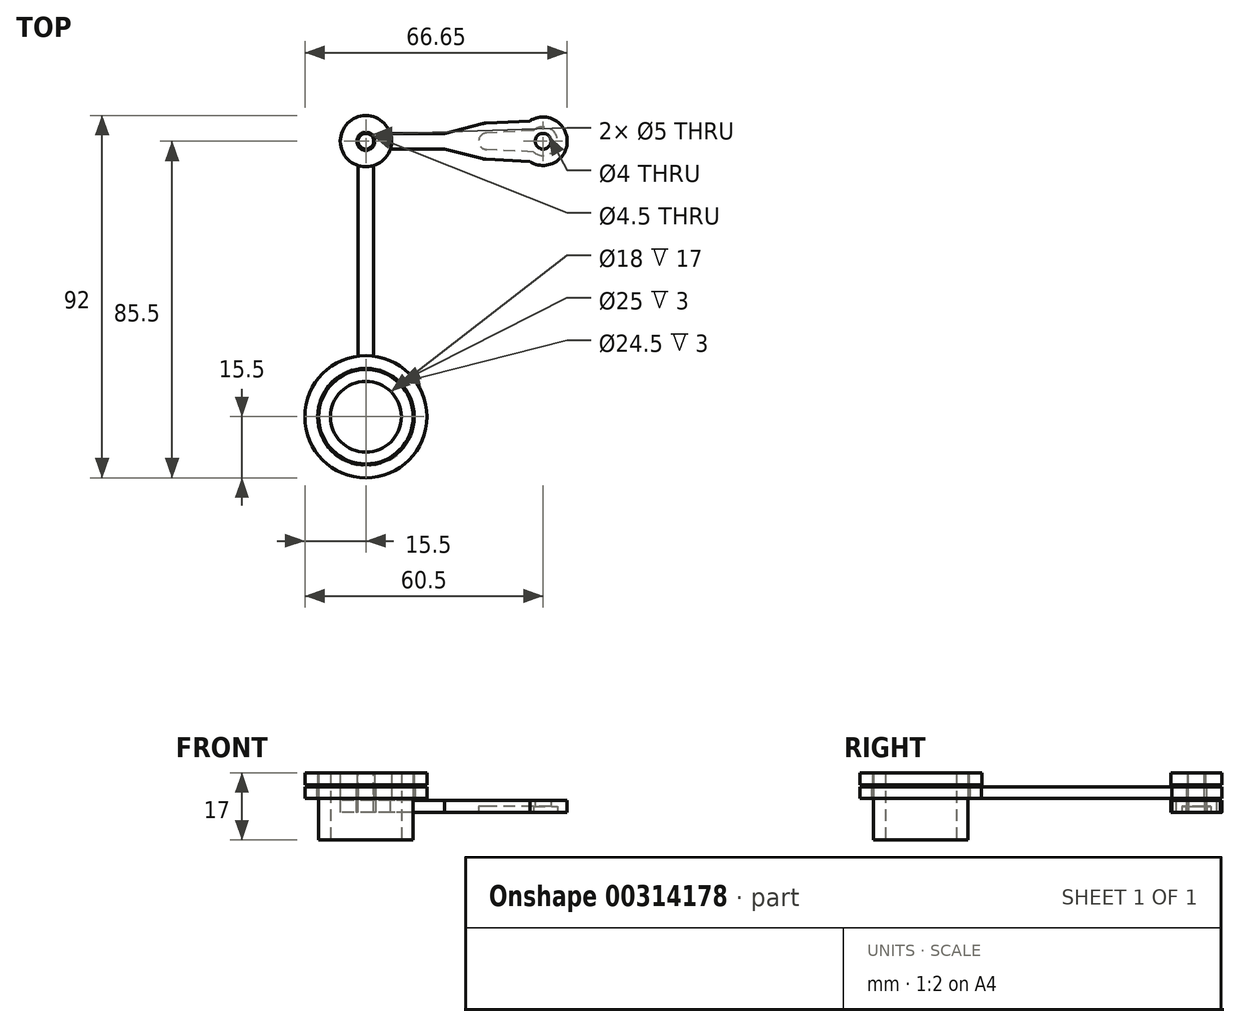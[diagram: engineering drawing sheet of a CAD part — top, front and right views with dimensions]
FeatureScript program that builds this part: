
annotation { "Feature Type Name" : "Feature", "Feature Type Description" : "" }
export const myFeature = defineFeature(function(context is Context, id is Id, definition is map)
    precondition{}
    {
        {
            var Q0;
            Q0=qCreatedBy(makeId("Top.planeOp"),FACE);
            cPlane(context, id + "F0", {"entities" : qUnion([Q0]), "cplaneType" : CPlaneType.OFFSET, "offset" : 3 * mm, "width" : 150 * mm, "height" : 150 * mm});
        }
        {
            var Q0;
            Q0=qCreatedBy(id+"F0.planeOp",FACE);
            cPlane(context, id + "F1", {"entities" : qUnion([Q0]), "cplaneType" : CPlaneType.OFFSET, "offset" : .5 * mm, "width" : 150 * mm, "height" : 150 * mm});
        }
        {
            var Q0;
            Q0=qCreatedBy(id+"F1.planeOp",FACE);
            cPlane(context, id + "F2", {"entities" : qUnion([Q0]), "cplaneType" : CPlaneType.OFFSET, "offset" : 3 * mm, "width" : 150 * mm, "height" : 150 * mm});
        }
        {
            var Q0;
            Q0=qCreatedBy(id+"F2.planeOp",FACE);
            cPlane(context, id + "F3", {"entities" : qUnion([Q0]), "cplaneType" : CPlaneType.OFFSET, "offset" : .5 * mm, "width" : 150 * mm, "height" : 150 * mm});
        }
        {
            var Q0;
            Q0=qCreatedBy(id+"F3.planeOp",FACE);
            cPlane(context, id + "F4", {"entities" : qUnion([Q0]), "cplaneType" : CPlaneType.OFFSET, "offset" : 3 * mm, "width" : 150 * mm, "height" : 150 * mm});
        }
        {
            var Q0;
            Q0=qCreatedBy(makeId("Top.planeOp"),FACE);
            var sketch = newSketch(context, id + "F5", { "sketchPlane" : qUnion([Q0])});
            skArc(sketch, "E0", {"start": v(-2.46, -2.7) * mm, "mid": v(3.65, 0) * mm, "end": v(-2.46, 2.7) * mm});
            skArc(sketch, "E1", {"start": v(-14.36, 2.1) * mm, "mid": v(-16.35, 0) * mm, "end": v(-14.36, -2.1) * mm});
            skPoint(sketch, "E2", {"position": v(-16.35, 0) * mm});
            skPoint(sketch, "E3", {"position": v(3.65, 0) * mm});
            skPoint(sketch, "E4", {"position": v(-2.46, 2.7) * mm});
            skPoint(sketch, "E5.MirrorP", {"position": v(-2.46, -2.7) * mm});
            skLineSegment(sketch, "E6", {"start": v(-2.46, 2.7) * mm, "end": v(-14.36, 2.1) * mm});
            skLineSegment(sketch, "E7", {"start": v(-2.46, -2.7) * mm, "end": v(-14.36, -2.1) * mm});
            skLineSegment(sketch, "E8.0", {"start": v(-3.35, 5.16) * mm, "end": v(-14.48, 4.6) * mm});
            skArc(sketch, "E8.1", {"start": v(-3.35, -5.16) * mm, "mid": v(6.15, 0) * mm, "end": v(-3.35, 5.16) * mm});
            skLineSegment(sketch, "E8.2", {"start": v(-3.35, -5.16) * mm, "end": v(-14.48, -4.6) * mm});
            skArc(sketch, "E8.3", {"start": v(-14.48, 4.6) * mm, "mid": v(-14.94, 4.55) * mm, "end": v(-15.39, 4.46) * mm});
            skLineSegment(sketch, "E9", {"start": v(-25, 0) * mm, "end": v(-25, 2) * mm, "construction": true});
            skLineSegment(sketch, "E10.MirrorCS", {"start": v(-25, 0) * mm, "end": v(-25, -2) * mm, "construction": true});
            skLineSegment(sketch, "E11", {"start": v(-25, 2) * mm, "end": v(-15.39, 4.46) * mm});
            skLineSegment(sketch, "E12", {"start": v(-25, -2) * mm, "end": v(-15.39, -4.46) * mm});
            skCircle(sketch, "E13", {"center": v(-45, 0) * mm, "radius": 2 * mm, "construction": true});
            skLineSegment(sketch, "E14", {"start": v(-25, 2) * mm, "end": v(-38.82, 2) * mm});
            skLineSegment(sketch, "E15.MirrorCS", {"start": v(-25, -2) * mm, "end": v(-38.82, -2) * mm});
            skArc(sketch, "E16.trimOffspring", {"start": v(-15.39, -4.46) * mm, "mid": v(-14.94, -4.55) * mm, "end": v(-14.48, -4.6) * mm});
            skCircle(sketch, "E17", {"center": v(0, 0) * mm, "radius": 2 * mm});
            skCircle(sketch, "E18", {"center": v(-45, 0) * mm, "radius": 2.5 * mm});
            skArc(sketch, "E19", {"start": v(-38.82, 2) * mm, "mid": v(-51.5, 0) * mm, "end": v(-38.82, -2) * mm});
            skArc(sketch, "E20", {"start": v(-38.82, -2) * mm, "mid": v(-38.5, 0) * mm, "end": v(-38.82, 2) * mm, "construction": true});
            skCircle(sketch, "E21", {"center": v(-45, -70) * mm, "radius": 9 * mm});
            skCircle(sketch, "E22", {"center": v(-45, -70) * mm, "radius": 12 * mm});
            skCircle(sketch, "E23", {"center": v(-45, -70) * mm, "radius": 15.5 * mm});
            skLineSegment(sketch, "E24", {"start": v(-45, 0) * mm, "end": v(-45, -70) * mm, "construction": true});
            skLineSegment(sketch, "E25", {"start": v(-47, -6.18) * mm, "end": v(-47, -54.63) * mm, "construction": true});
            skLineSegment(sketch, "E26.MirrorCS", {"start": v(-43, -6.18) * mm, "end": v(-43, -54.63) * mm, "construction": true});
            skCircle(sketch, "E27", {"center": v(-45, -70) * mm, "radius": 12.5 * mm});
            skCircle(sketch, "E28", {"center": v(-45, -70) * mm, "radius": 12.25 * mm, "construction": true});
            skSolve(sketch);
        }
        {
            var Q0;
            Q0=makeQuery(id+"F5.imprint","IMPRINT",FACE,{"disambiguationData":[TD([[makeQuery(id+"F5.imprint","IMPRINT",EDGE,{"derivedFrom":sQuery(id+"F5.wireOp",EDGE,"E0")}),-1.0]])]});
            var Q1;
            Q1=makeQuery(id+"F5.imprint","IMPRINT",FACE,{"disambiguationData":[TD([[makeQuery(id+"F5.imprint","IMPRINT",EDGE,{"derivedFrom":sQuery(id+"F5.wireOp",EDGE,"E0")}),1.0]])]});
            var Q2;
            Q2=qCreatedBy(id+"F0.planeOp",FACE);
            extrude(context, id + "F6", {"entities" : qUnion([Q0, Q1]), "endBound" : BoundingType.UP_TO_SURFACE, "endBoundEntityFace" : qUnion([Q2]), "depth" : 3 * mm});
        }
        {
            var Q0;
            Q0=makeQuery(id+"F5.imprint","IMPRINT",FACE,{"disambiguationData":[TD([[makeQuery(id+"F5.imprint","IMPRINT",EDGE,{"derivedFrom":sQuery(id+"F5.wireOp",EDGE,"E0")}),1.0]])]});
            extrude(context, id + "F7", {"entities" : qUnion([Q0]), "operationType" : NewBodyOperationType.REMOVE, "depth" : 1.5 * mm});
        }
        {
            var Q0;
            Q0=qCreatedBy(id+"F1.planeOp",FACE);
            var sketch = newSketch(context, id + "F8", { "sketchPlane" : qUnion([Q0])});
            skArc(sketch, "E29.0", {"start": v(-38.82, 2) * mm, "mid": v(-49.6, 4.6) * mm, "end": v(-47, -6.18) * mm});
            skArc(sketch, "E29.1", {"start": v(-38.82, -2) * mm, "mid": v(-38.5, 0) * mm, "end": v(-38.82, 2) * mm});
            skLineSegment(sketch, "E29.2", {"start": v(-43, -6.18) * mm, "end": v(-43, -54.63) * mm});
            skLineSegment(sketch, "E29.3", {"start": v(-47, -6.18) * mm, "end": v(-47, -54.63) * mm});
            skArc(sketch, "E29.4", {"start": v(-47, -54.63) * mm, "mid": v(-45, -85.5) * mm, "end": v(-43, -54.63) * mm});
            skArc(sketch, "E30.trimOffspring", {"start": v(-43, -6.18) * mm, "mid": v(-40.4, -4.6) * mm, "end": v(-38.82, -2) * mm});
            skCircle(sketch, "E31.0", {"center": v(-45, 0) * mm, "radius": 2.5 * mm});
            skCircle(sketch, "E32.0", {"center": v(-45, -70) * mm, "radius": 12.5 * mm});
            skSolve(sketch);
        }
        {
            var Q0;
            Q0=makeQuery(id+"F8.imprint","IMPRINT",FACE,{"disambiguationData":[TD([[makeQuery(id+"F8.imprint","IMPRINT",EDGE,{"derivedFrom":sQuery(id+"F8.wireOp",EDGE,"E29.0")}),1.0]])]});
            var Q1;
            Q1=qCreatedBy(id+"F2.planeOp",FACE);
            extrude(context, id + "F9", {"entities" : qUnion([Q0]), "endBound" : BoundingType.UP_TO_SURFACE, "endBoundEntityFace" : qUnion([Q1]), "depth" : 4 * mm});
        }
        {
            var Q0;
            Q0=qCreatedBy(id+"F3.planeOp",FACE);
            var sketch = newSketch(context, id + "F10", { "sketchPlane" : qUnion([Q0])});
            skArc(sketch, "E33.0", {"start": v(-38.82, -2) * mm, "mid": v(-38.5, 0) * mm, "end": v(-38.82, 2) * mm});
            skArc(sketch, "E33.1", {"start": v(-38.82, 2) * mm, "mid": v(-51.5, 0) * mm, "end": v(-38.82, -2) * mm});
            skCircle(sketch, "E33.2", {"center": v(-45, 0) * mm, "radius": 2 * mm});
            skCircle(sketch, "E34", {"center": v(-45, 0) * mm, "radius": 2.25 * mm});
            skSolve(sketch);
        }
        {
            var Q0;
            Q0 = qSketchRegion(id + "F10", true);
            extrude(context, id + "F11", {"entities" : qUnion([Q0]), "depth" : 3 * mm});
        }
        {
            var Q0;
            Q0=makeQuery(id+"F10.imprint","IMPRINT",FACE,{"disambiguationData":[TD([[makeQuery(id+"F10.imprint","IMPRINT",EDGE,{"derivedFrom":sQuery(id+"F10.wireOp",EDGE,"E33.2")}),1.0]])]});
            var Q1;
            Q1=sQuery(id+"F10.wireOp",EDGE,"E33.2");
            var Q2;
            Q2=makeQuery(id+"F6.opExtrude","CAP_FACE",FACE,{"disambiguationData":[OSD([sQuery(id+"F5.wireOp",EDGE,"E8.0"),sQuery(id+"F5.wireOp",EDGE,"E8.1"),sQuery(id+"F5.wireOp",EDGE,"E8.2"),sQuery(id+"F5.wireOp",EDGE,"E8.3"),sQuery(id+"F5.wireOp",EDGE,"E11"),sQuery(id+"F5.wireOp",EDGE,"E12"),sQuery(id+"F5.wireOp",EDGE,"E14"),sQuery(id+"F5.wireOp",EDGE,"E15.MirrorCS"),sQuery(id+"F5.wireOp",EDGE,"E16.trimOffspring"),sQuery(id+"F5.wireOp",EDGE,"E17"),sQuery(id+"F5.wireOp",EDGE,"E18"),sQuery(id+"F5.wireOp",EDGE,"E19")])],"isStart":true});
            extrude(context, id + "F12", {"entities" : qUnion([Q0]), "operationType" : NewBodyOperationType.ADD, "surfaceEntities" : qUnion([Q1]), "endBound" : BoundingType.UP_TO_SURFACE, "oppositeDirection" : true, "endBoundEntityFace" : qUnion([Q2]), "depth" : 25 * mm});
        }
        {
            var Q0;
            Q0=makeQuery(id+"F5.imprint","IMPRINT",FACE,{"disambiguationData":[TD([[makeQuery(id+"F5.imprint","IMPRINT",EDGE,{"derivedFrom":sQuery(id+"F5.wireOp",EDGE,"E21")}),-1.0]])]});
            var Q1;
            Q1=qCreatedBy(id+"F4.planeOp",FACE);
            extrude(context, id + "F13", {"entities" : qUnion([Q0]), "endBound" : BoundingType.UP_TO_SURFACE, "endBoundEntityFace" : qUnion([Q1]), "depth" : 25 * mm});
        }
        {
            var Q0;
            Q0=qCreatedBy(id+"F3.planeOp",FACE);
            var sketch = newSketch(context, id + "F14", { "sketchPlane" : qUnion([Q0])});
            skCircle(sketch, "E35.1", {"center": v(-45, -70) * mm, "radius": 15.5 * mm});
            skCircle(sketch, "E36.0", {"center": v(-45, -70) * mm, "radius": 12.25 * mm});
            skSolve(sketch);
        }
        {
            var Q0;
            Q0=makeQuery(id+"F14.imprint","IMPRINT",FACE,{"disambiguationData":[TD([[makeQuery(id+"F14.imprint","IMPRINT",EDGE,{"derivedFrom":sQuery(id+"F14.wireOp",EDGE,"E35.1")}),1.0]])]});
            var Q1;
            Q1=qCreatedBy(id+"F4.planeOp",FACE);
            extrude(context, id + "F15", {"entities" : qUnion([Q0]), "endBound" : BoundingType.UP_TO_SURFACE, "endBoundEntityFace" : qUnion([Q1]), "depth" : 25 * mm});
        }
        {
            var Q0;
            Q0=qCreatedBy(makeId("Top.planeOp"),FACE);
            cPlane(context, id + "F16", {"entities" : qUnion([Q0]), "cplaneType" : CPlaneType.OFFSET, "offset" : 7 * mm, "oppositeDirection" : true, "width" : 150 * mm, "height" : 150 * mm});
        }
        {
            var Q0;
            Q0=makeQuery(id+"F5.imprint","IMPRINT",FACE,{"disambiguationData":[TD([[makeQuery(id+"F5.imprint","IMPRINT",EDGE,{"derivedFrom":sQuery(id+"F5.wireOp",EDGE,"E21")}),-1.0]])]});
            var Q1;
            Q1=qCreatedBy(id+"F16.planeOp",FACE);
            extrude(context, id + "F17", {"entities" : qUnion([Q0]), "operationType" : NewBodyOperationType.ADD, "endBound" : BoundingType.UP_TO_SURFACE, "oppositeDirection" : true, "endBoundEntityFace" : qUnion([Q1]), "depth" : 25 * mm});
        }
        {
            var Q0;
            Q0=makeQuery(id+"F12.opExtrude","CAP_FACE",FACE,{"disambiguationData":[OSD([sQuery(id+"F10.wireOp",EDGE,"E33.2")])],"isStart":true});
            var Q1;
            Q1=makeQuery(id+"F11.opExtrude","CAP_FACE",FACE,{"disambiguationData":[OSD([sQuery(id+"F10.wireOp",EDGE,"E33.0"),sQuery(id+"F10.wireOp",EDGE,"E33.1"),sQuery(id+"F10.wireOp",EDGE,"E34")])],"isStart":false});
            extrude(context, id + "F18", {"entities" : qUnion([Q0]), "operationType" : NewBodyOperationType.ADD, "endBound" : BoundingType.UP_TO_SURFACE, "endBoundEntityFace" : qUnion([Q1]), "depth" : 25 * mm});
        }
    });
